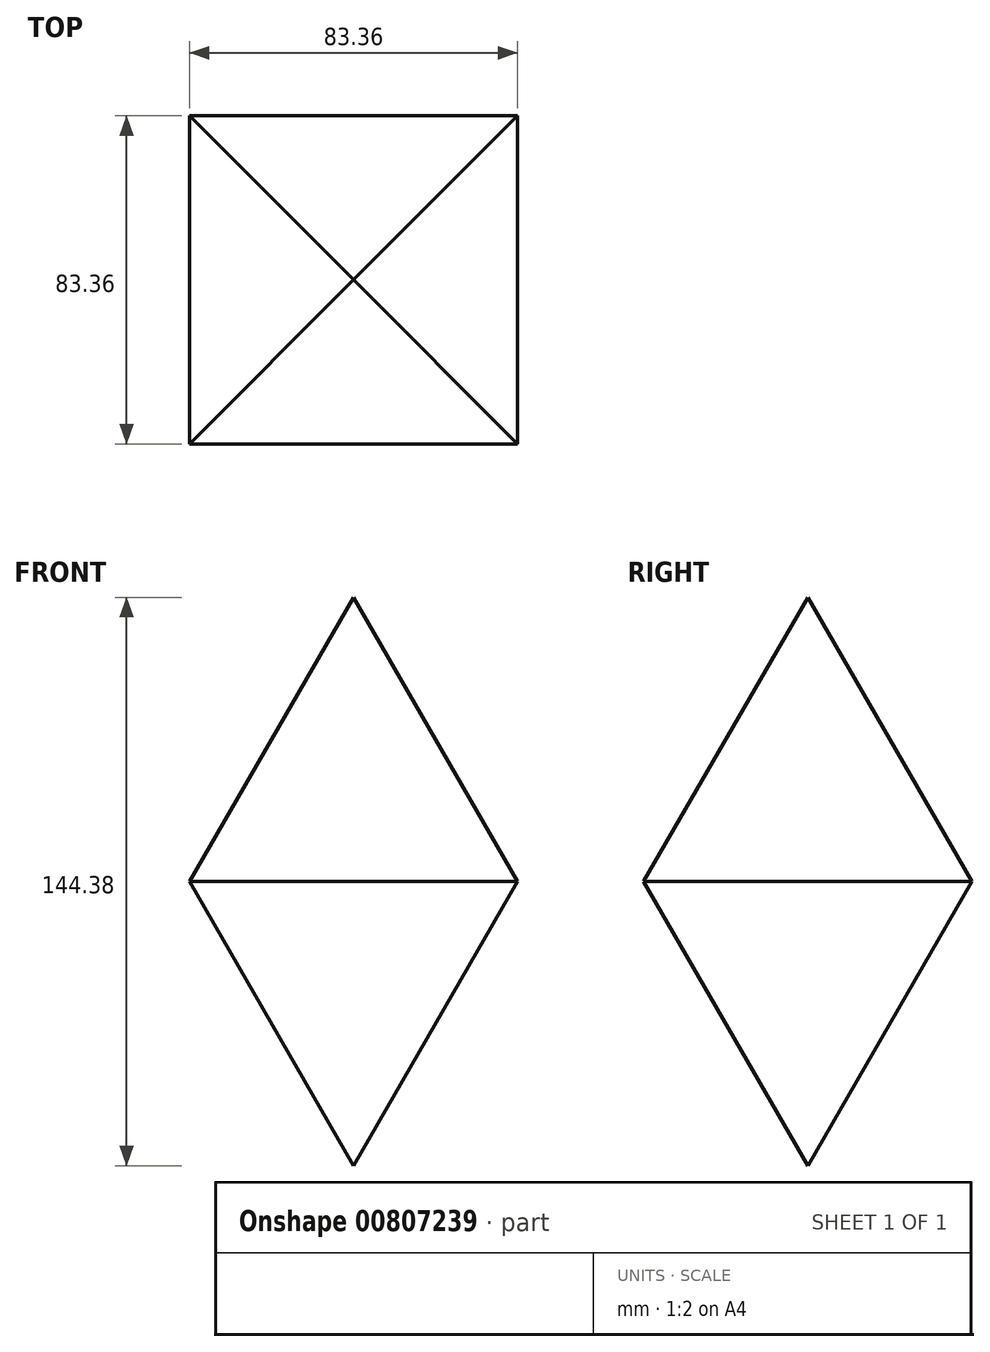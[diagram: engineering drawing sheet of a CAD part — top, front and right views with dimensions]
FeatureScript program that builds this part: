
annotation { "Feature Type Name" : "Feature", "Feature Type Description" : "" }
export const myFeature = defineFeature(function(context is Context, id is Id, definition is map)
    precondition{}
    {
        {
            var Q0;
            Q0=qCreatedBy(makeId("Top.planeOp"),FACE);
            var sketch = newSketch(context, id + "F0", { "sketchPlane" : qUnion([Q0])});
            skLineSegment(sketch, "E0.bottom", {"start": v(-41.68, -41.68) * mm, "end": v(41.68, -41.68) * mm});
            skLineSegment(sketch, "E0.top", {"start": v(-41.68, 41.68) * mm, "end": v(41.68, 41.68) * mm});
            skLineSegment(sketch, "E0.left", {"start": v(-41.68, -41.68) * mm, "end": v(-41.68, 41.68) * mm});
            skLineSegment(sketch, "E0.right", {"start": v(41.68, -41.68) * mm, "end": v(41.68, 41.68) * mm});
            skPoint(sketch, "E0.middle", {"position": v(0, 0) * mm});
            skSolve(sketch);
        }
        {
            var Q0;
            Q0=makeQuery(id+"F0.imprint","IMPRINT",FACE,{"disambiguationData":[TD([[makeQuery(id+"F0.imprint","IMPRINT",EDGE,{"derivedFrom":sQuery(id+"F0.wireOp",EDGE,"E0.bottom")}),1.0]])]});
            extrude(context, id + "F1", {"entities" : qUnion([Q0]), "depth" : 151.13 * mm, "offsetDistance" : 25.4 * mm, "hasDraft" : true, "draftAngle" : 30 * degree, "draftPullDirection" : true, "hasSecondDirection" : true, "secondDirectionOppositeDirection" : true, "secondDirectionDepth" : 91.7 * mm, "hasSecondDirectionDraft" : true, "secondDirectionDraftAngle" : 30 * degree, "secondDirectionDraftPullDirection" : true});
        }
    });
